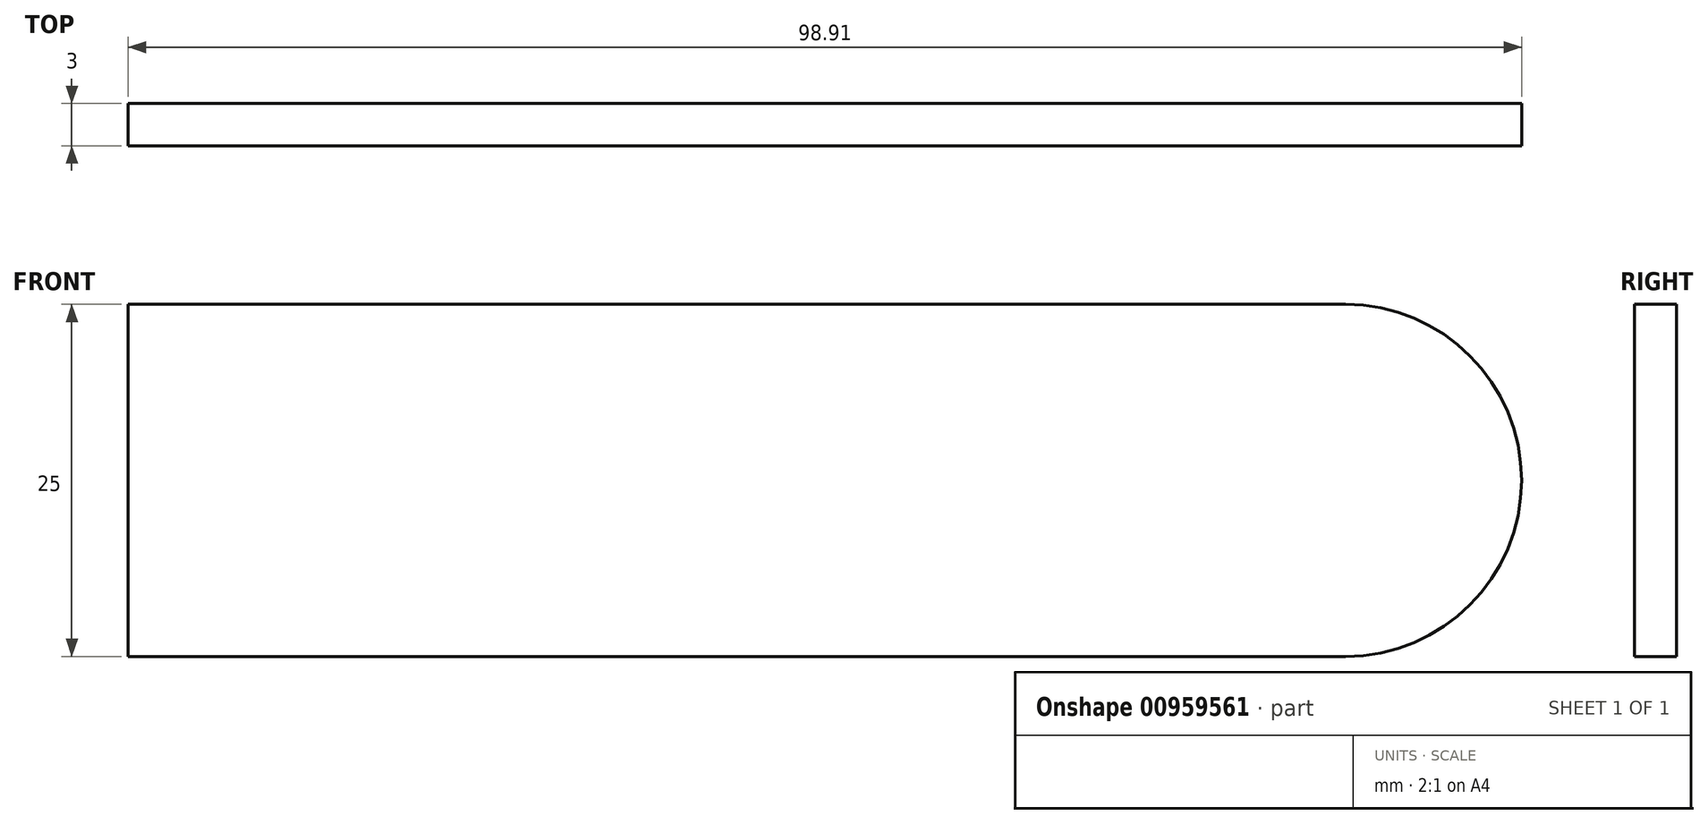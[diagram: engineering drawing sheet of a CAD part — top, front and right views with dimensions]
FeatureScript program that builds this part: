
annotation { "Feature Type Name" : "Feature", "Feature Type Description" : "" }
export const myFeature = defineFeature(function(context is Context, id is Id, definition is map)
    precondition{}
    {
        {
            var Q0;
            Q0=qCreatedBy(makeId("Front.planeOp"),FACE);
            var sketch = newSketch(context, id + "F0", { "sketchPlane" : qUnion([Q0])});
            skLineSegment(sketch, "E0.bottom", {"start": v(50, 12.5) * mm, "end": v(-50, 12.5) * mm});
            skLineSegment(sketch, "E0.top", {"start": v(50, -12.5) * mm, "end": v(-50, -12.5) * mm});
            skLineSegment(sketch, "E0.left", {"start": v(50, 12.5) * mm, "end": v(50, -12.5) * mm});
            skLineSegment(sketch, "E0.right", {"start": v(-50, 12.5) * mm, "end": v(-50, -12.5) * mm});
            skPoint(sketch, "E0.middle", {"position": v(0, 0) * mm});
            skSolve(sketch);
        }
        {
            var Q0;
            Q0=makeQuery(id+"F0.imprint","IMPRINT",FACE,{"disambiguationData":[TD([[makeQuery(id+"F0.imprint","IMPRINT",EDGE,{"derivedFrom":sQuery(id+"F0.wireOp",EDGE,"E0.bottom")}),1.0]])]});
            extrude(context, id + "F1", {"entities" : qUnion([Q0]), "depth" : 3 * mm, "offsetDistance" : 25 * mm});
        }
        {
            var Q0;
            Q0=makeQuery(id+"F1.opExtrude","CAP_FACE",FACE,{"disambiguationData":[OSD([sQuery(id+"F0.wireOp",EDGE,"E0.bottom"),sQuery(id+"F0.wireOp",EDGE,"E0.top"),sQuery(id+"F0.wireOp",EDGE,"E0.left"),sQuery(id+"F0.wireOp",EDGE,"E0.right")])],"isStart":false});
            var sketch = newSketch(context, id + "F2", { "sketchPlane" : qUnion([Q0])});
            skArc(sketch, "E1", {"start": v(36.4, -12.5) * mm, "mid": v(48.9, 0) * mm, "end": v(36.4, 12.5) * mm});
            skSolve(sketch);
        }
        {
            var Q0;
            {var subQ0=sQuery(id+"F2.wireOp",EDGE,"E1");Q0=makeQuery(id+"F2.imprint","IMPRINT",FACE,{"disambiguationData":[TD([[makeQuery(id+"F2.imprint","IMPRINT",EDGE,{"derivedFrom":subQ0}),-1.0]])]});}
            extrude(context, id + "F3", {"entities" : qUnion([Q0]), "operationType" : NewBodyOperationType.REMOVE, "endBound" : BoundingType.THROUGH_ALL, "oppositeDirection" : true, "depth" : 25 * mm, "offsetDistance" : 25 * mm});
        }
    });
